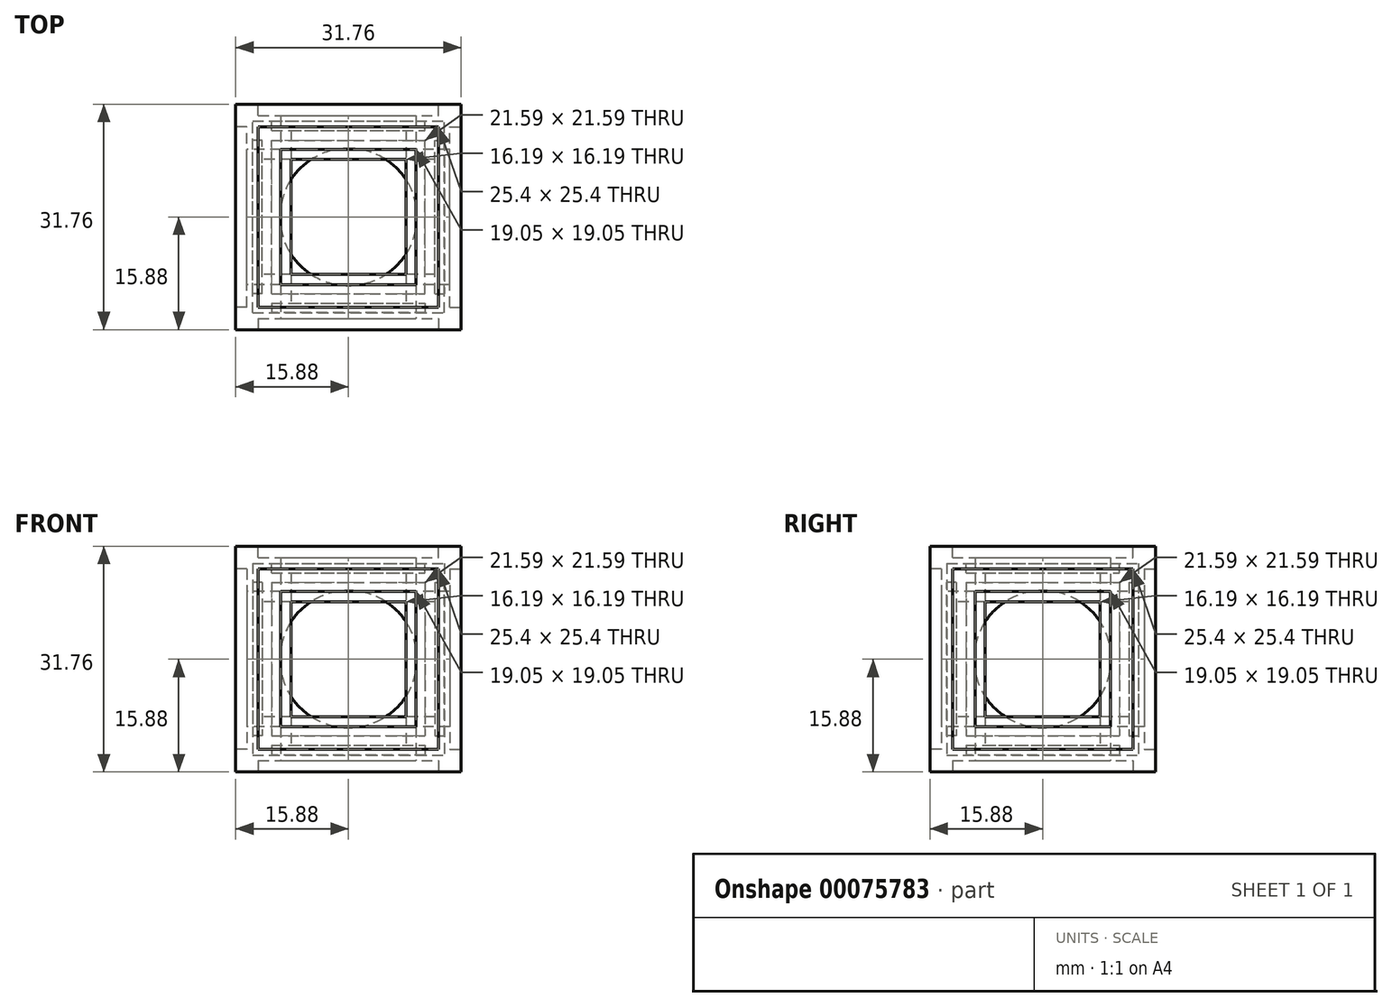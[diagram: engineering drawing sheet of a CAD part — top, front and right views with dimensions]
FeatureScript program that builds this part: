
annotation { "Feature Type Name" : "Feature", "Feature Type Description" : "" }
export const myFeature = defineFeature(function(context is Context, id is Id, definition is map)
    precondition{}
    {
        {
            var Q0;
            Q0=qCreatedBy(makeId("Top.planeOp"),FACE);
            var sketch = newSketch(context, id + "F0", { "sketchPlane" : qUnion([Q0])});
            skLineSegment(sketch, "E0.bottom", {"start": v(0, 0) * mm, "end": v(31.75, 0) * mm});
            skLineSegment(sketch, "E0.top", {"start": v(0, 31.75) * mm, "end": v(31.75, 31.75) * mm});
            skLineSegment(sketch, "E0.left", {"start": v(0, 0) * mm, "end": v(0, 31.75) * mm});
            skLineSegment(sketch, "E0.right", {"start": v(31.75, 0) * mm, "end": v(31.75, 31.75) * mm});
            skSolve(sketch);
        }
        {
            var Q0;
            Q0=makeQuery(id+"F0.imprint","IMPRINT",FACE,{"disambiguationData":[TD([[makeQuery(id+"F0.imprint","IMPRINT",EDGE,{"derivedFrom":sQuery(id+"F0.wireOp",EDGE,"E0.bottom")}),1.0]])]});
            extrude(context, id + "F1", {"entities" : qUnion([Q0]), "depth" : 31.75 * mm});
        }
        {
            var Q0;
            Q0=makeQuery(id+"F1.opExtrude","SWEPT_FACE",FACE,{"disambiguationData":[OSD([sQuery(id+"F0.wireOp",EDGE,"E0.bottom")])]});
            var sketch = newSketch(context, id + "F2", { "sketchPlane" : qUnion([Q0])});
            skLineSegment(sketch, "E1.0", {"start": v(28.57, 28.57) * mm, "end": v(28.57, 3.18) * mm});
            skLineSegment(sketch, "E1.1", {"start": v(3.18, 28.57) * mm, "end": v(28.57, 28.57) * mm});
            skLineSegment(sketch, "E1.2", {"start": v(3.18, 28.57) * mm, "end": v(3.18, 3.18) * mm});
            skLineSegment(sketch, "E1.3", {"start": v(3.18, 3.18) * mm, "end": v(28.57, 3.18) * mm});
            skLineSegment(sketch, "E2.0", {"start": v(25.4, 25.4) * mm, "end": v(25.4, 6.35) * mm});
            skLineSegment(sketch, "E2.1", {"start": v(6.35, 25.4) * mm, "end": v(25.4, 25.4) * mm});
            skLineSegment(sketch, "E2.2", {"start": v(6.35, 25.4) * mm, "end": v(6.35, 6.35) * mm});
            skLineSegment(sketch, "E2.3", {"start": v(6.35, 6.35) * mm, "end": v(25.4, 6.35) * mm});
            skSolve(sketch);
        }
        {
            var Q0;
            Q0=makeQuery(id+"F1.opExtrude","CAP_FACE",FACE,{"disambiguationData":[OSD([sQuery(id+"F0.wireOp",EDGE,"E0.bottom"),sQuery(id+"F0.wireOp",EDGE,"E0.top"),sQuery(id+"F0.wireOp",EDGE,"E0.left"),sQuery(id+"F0.wireOp",EDGE,"E0.right")])],"isStart":false});
            var sketch = newSketch(context, id + "F3", { "sketchPlane" : qUnion([Q0])});
            skLineSegment(sketch, "E3.0", {"start": v(28.58, 3.18) * mm, "end": v(28.57, 28.57) * mm});
            skLineSegment(sketch, "E3.1", {"start": v(3.18, 3.18) * mm, "end": v(28.58, 3.18) * mm});
            skLineSegment(sketch, "E3.2", {"start": v(3.18, 3.18) * mm, "end": v(3.18, 28.57) * mm});
            skLineSegment(sketch, "E3.3", {"start": v(3.18, 28.57) * mm, "end": v(28.57, 28.57) * mm});
            skLineSegment(sketch, "E4.0", {"start": v(6.35, 25.4) * mm, "end": v(25.4, 25.4) * mm});
            skLineSegment(sketch, "E4.1", {"start": v(6.35, 6.35) * mm, "end": v(6.35, 25.4) * mm});
            skLineSegment(sketch, "E4.2", {"start": v(6.35, 6.35) * mm, "end": v(25.4, 6.35) * mm});
            skLineSegment(sketch, "E4.3", {"start": v(25.4, 6.35) * mm, "end": v(25.4, 25.4) * mm});
            skSolve(sketch);
        }
        {
            var Q0;
            Q0=makeQuery(id+"F1.opExtrude","SWEPT_FACE",FACE,{"disambiguationData":[OSD([sQuery(id+"F0.wireOp",EDGE,"E0.right")])]});
            var sketch = newSketch(context, id + "F4", { "sketchPlane" : qUnion([Q0])});
            skLineSegment(sketch, "E5.0", {"start": v(28.57, 28.57) * mm, "end": v(28.57, 3.18) * mm});
            skLineSegment(sketch, "E5.1", {"start": v(3.17, 28.57) * mm, "end": v(28.57, 28.57) * mm});
            skLineSegment(sketch, "E5.2", {"start": v(3.17, 28.57) * mm, "end": v(3.17, 3.18) * mm});
            skLineSegment(sketch, "E5.3", {"start": v(3.17, 3.18) * mm, "end": v(28.57, 3.18) * mm});
            skLineSegment(sketch, "E6.0", {"start": v(25.4, 25.4) * mm, "end": v(25.4, 6.35) * mm});
            skLineSegment(sketch, "E6.1", {"start": v(6.35, 25.4) * mm, "end": v(25.4, 25.4) * mm});
            skLineSegment(sketch, "E6.2", {"start": v(6.35, 25.4) * mm, "end": v(6.35, 6.35) * mm});
            skLineSegment(sketch, "E6.3", {"start": v(6.35, 6.35) * mm, "end": v(25.4, 6.35) * mm});
            skSolve(sketch);
        }
        {
            var Q0;
            Q0=makeQuery(id+"F1.opExtrude","SWEPT_FACE",FACE,{"disambiguationData":[OSD([sQuery(id+"F0.wireOp",EDGE,"E0.top")])]});
            var sketch = newSketch(context, id + "F5", { "sketchPlane" : qUnion([Q0])});
            skLineSegment(sketch, "E7.0", {"start": v(-3.18, 28.57) * mm, "end": v(-3.18, 3.18) * mm});
            skLineSegment(sketch, "E7.1", {"start": v(-3.18, 28.57) * mm, "end": v(-28.57, 28.57) * mm});
            skLineSegment(sketch, "E7.2", {"start": v(-28.57, 28.57) * mm, "end": v(-28.57, 3.18) * mm});
            skLineSegment(sketch, "E7.3", {"start": v(-3.18, 3.18) * mm, "end": v(-28.57, 3.18) * mm});
            skLineSegment(sketch, "E8.0", {"start": v(-6.35, 25.4) * mm, "end": v(-6.35, 6.35) * mm});
            skLineSegment(sketch, "E8.1", {"start": v(-6.35, 25.4) * mm, "end": v(-25.4, 25.4) * mm});
            skLineSegment(sketch, "E8.2", {"start": v(-25.4, 25.4) * mm, "end": v(-25.4, 6.35) * mm});
            skLineSegment(sketch, "E8.3", {"start": v(-6.35, 6.35) * mm, "end": v(-25.4, 6.35) * mm});
            skSolve(sketch);
        }
        {
            var Q0;
            Q0=makeQuery(id+"F1.opExtrude","SWEPT_FACE",FACE,{"disambiguationData":[OSD([sQuery(id+"F0.wireOp",EDGE,"E0.left")])]});
            var sketch = newSketch(context, id + "F6", { "sketchPlane" : qUnion([Q0])});
            skLineSegment(sketch, "E9.0", {"start": v(-3.18, 28.57) * mm, "end": v(-28.57, 28.57) * mm});
            skLineSegment(sketch, "E9.1", {"start": v(-3.18, 28.57) * mm, "end": v(-3.18, 3.18) * mm});
            skLineSegment(sketch, "E9.2", {"start": v(-3.18, 3.18) * mm, "end": v(-28.57, 3.18) * mm});
            skLineSegment(sketch, "E9.3", {"start": v(-28.57, 28.57) * mm, "end": v(-28.57, 3.18) * mm});
            skLineSegment(sketch, "E10.0", {"start": v(-6.35, 25.4) * mm, "end": v(-25.4, 25.4) * mm});
            skLineSegment(sketch, "E10.1", {"start": v(-6.35, 25.4) * mm, "end": v(-6.35, 6.35) * mm});
            skLineSegment(sketch, "E10.2", {"start": v(-6.35, 6.35) * mm, "end": v(-25.4, 6.35) * mm});
            skLineSegment(sketch, "E10.3", {"start": v(-25.4, 25.4) * mm, "end": v(-25.4, 6.35) * mm});
            skSolve(sketch);
        }
        {
            var Q0;
            Q0=makeQuery(id+"F0.imprint","IMPRINT",FACE,{"disambiguationData":[TD([[makeQuery(id+"F0.imprint","IMPRINT",EDGE,{"derivedFrom":sQuery(id+"F0.wireOp",EDGE,"E0.bottom")}),1.0]])]});
            var sketch = newSketch(context, id + "F7", { "sketchPlane" : qUnion([Q0])});
            skLineSegment(sketch, "E11.0", {"start": v(3.18, 3.18) * mm, "end": v(28.58, 3.18) * mm});
            skLineSegment(sketch, "E11.1", {"start": v(3.18, 3.18) * mm, "end": v(3.18, 28.57) * mm});
            skLineSegment(sketch, "E11.2", {"start": v(3.18, 28.57) * mm, "end": v(28.57, 28.57) * mm});
            skLineSegment(sketch, "E11.3", {"start": v(28.58, 3.18) * mm, "end": v(28.57, 28.57) * mm});
            skLineSegment(sketch, "E12.0", {"start": v(6.35, 6.35) * mm, "end": v(25.4, 6.35) * mm});
            skLineSegment(sketch, "E12.1", {"start": v(6.35, 6.35) * mm, "end": v(6.35, 25.4) * mm});
            skLineSegment(sketch, "E12.2", {"start": v(6.35, 25.4) * mm, "end": v(25.4, 25.4) * mm});
            skLineSegment(sketch, "E12.3", {"start": v(25.4, 6.35) * mm, "end": v(25.4, 25.4) * mm});
            skSolve(sketch);
        }
        {
            var Q0;
            Q0=makeQuery(id+"F6.imprint","IMPRINT",FACE,{"disambiguationData":[TD([[makeQuery(id+"F6.imprint","IMPRINT",EDGE,{"derivedFrom":sQuery(id+"F6.wireOp",EDGE,"E10.0")}),1.0]])]});
            extrude(context, id + "F8", {"entities" : qUnion([Q0]), "operationType" : NewBodyOperationType.REMOVE, "endBound" : BoundingType.THROUGH_ALL, "oppositeDirection" : true, "depth" : 25.4 * mm});
        }
        {
            var Q0;
            Q0=makeQuery(id+"F2.imprint","IMPRINT",FACE,{"disambiguationData":[TD([[makeQuery(id+"F2.imprint","IMPRINT",EDGE,{"derivedFrom":sQuery(id+"F2.wireOp",EDGE,"E2.0")}),-1.0]])]});
            extrude(context, id + "F9", {"entities" : qUnion([Q0]), "operationType" : NewBodyOperationType.REMOVE, "endBound" : BoundingType.THROUGH_ALL, "oppositeDirection" : true, "depth" : 25.4 * mm});
        }
        {
            var Q0;
            Q0=makeQuery(id+"F7.imprint","IMPRINT",FACE,{"disambiguationData":[TD([[makeQuery(id+"F7.imprint","IMPRINT",EDGE,{"derivedFrom":sQuery(id+"F7.wireOp",EDGE,"E12.0")}),1.0]])]});
            extrude(context, id + "F10", {"entities" : qUnion([Q0]), "operationType" : NewBodyOperationType.REMOVE, "endBound" : BoundingType.THROUGH_ALL, "depth" : 25.4 * mm});
        }
        {
            var Q0;
            Q0=makeQuery(id+"F2.imprint","IMPRINT",FACE,{"disambiguationData":[TD([[makeQuery(id+"F2.imprint","IMPRINT",EDGE,{"derivedFrom":sQuery(id+"F2.wireOp",EDGE,"E1.0")}),-1.0]])]});
            extrude(context, id + "F11", {"entities" : qUnion([Q0]), "operationType" : NewBodyOperationType.REMOVE, "endBound" : BoundingType.SYMMETRIC, "oppositeDirection" : true, "depth" : 3.17 * mm});
        }
        {
            var Q0;
            Q0=makeQuery(id+"F7.imprint","IMPRINT",FACE,{"disambiguationData":[TD([[makeQuery(id+"F7.imprint","IMPRINT",EDGE,{"derivedFrom":sQuery(id+"F7.wireOp",EDGE,"E11.0")}),1.0]])]});
            extrude(context, id + "F12", {"entities" : qUnion([Q0]), "operationType" : NewBodyOperationType.REMOVE, "endBound" : BoundingType.SYMMETRIC, "depth" : 3.17 * mm});
        }
        {
            var Q0;
            Q0=makeQuery(id+"F3.imprint","IMPRINT",FACE,{"disambiguationData":[TD([[makeQuery(id+"F3.imprint","IMPRINT",EDGE,{"derivedFrom":sQuery(id+"F3.wireOp",EDGE,"E3.0")}),1.0]])]});
            extrude(context, id + "F13", {"entities" : qUnion([Q0]), "operationType" : NewBodyOperationType.REMOVE, "endBound" : BoundingType.SYMMETRIC, "oppositeDirection" : true, "depth" : 3.17 * mm});
        }
        {
            var Q0;
            Q0=makeQuery(id+"F4.imprint","IMPRINT",FACE,{"disambiguationData":[TD([[makeQuery(id+"F4.imprint","IMPRINT",EDGE,{"derivedFrom":sQuery(id+"F4.wireOp",EDGE,"E5.0")}),-1.0]])]});
            extrude(context, id + "F14", {"entities" : qUnion([Q0]), "operationType" : NewBodyOperationType.REMOVE, "endBound" : BoundingType.SYMMETRIC, "oppositeDirection" : true, "depth" : 3.17 * mm});
        }
        {
            var Q0;
            Q0=makeQuery(id+"F5.imprint","IMPRINT",FACE,{"disambiguationData":[TD([[makeQuery(id+"F5.imprint","IMPRINT",EDGE,{"derivedFrom":sQuery(id+"F5.wireOp",EDGE,"E7.0")}),-1.0]])]});
            extrude(context, id + "F15", {"entities" : qUnion([Q0]), "operationType" : NewBodyOperationType.REMOVE, "endBound" : BoundingType.SYMMETRIC, "oppositeDirection" : true, "depth" : 3.17 * mm});
        }
        {
            var Q0;
            Q0=makeQuery(id+"F6.imprint","IMPRINT",FACE,{"disambiguationData":[TD([[makeQuery(id+"F6.imprint","IMPRINT",EDGE,{"derivedFrom":sQuery(id+"F6.wireOp",EDGE,"E9.0")}),1.0]])]});
            extrude(context, id + "F16", {"entities" : qUnion([Q0]), "operationType" : NewBodyOperationType.REMOVE, "endBound" : BoundingType.SYMMETRIC, "oppositeDirection" : true, "depth" : 3.17 * mm});
        }
        {
            var Q0;
            Q0=makeQuery(id+"F1.opExtrude","SWEPT_BODY",BODY,{"disambiguationData":[OSD([sQuery(id+"F0.wireOp",EDGE,"E0.bottom"),sQuery(id+"F0.wireOp",EDGE,"E0.top"),sQuery(id+"F0.wireOp",EDGE,"E0.left"),sQuery(id+"F0.wireOp",EDGE,"E0.right")])]});
            transform(context, id + "F17", {"entities" : qUnion([Q0]), "transformType" : TransformType.TRANSLATION_3D, "dx" : -15.88 * mm, "dy" : -15.88 * mm, "dz" : -15.88 * mm, "makeCopy" : false});
        }
        {
            var Q0;
            Q0=qCreatedBy(makeId("Top.planeOp"),FACE);
            var sketch = newSketch(context, id + "F18", { "sketchPlane" : qUnion([Q0])});
            skArc(sketch, "E13", {"start": v(0, -9.65) * mm, "mid": v(9.65, 0) * mm, "end": v(0, 9.65) * mm});
            skLineSegment(sketch, "E14", {"start": v(0, 9.65) * mm, "end": v(0, -9.65) * mm});
            skSolve(sketch);
        }
        {
            var Q0;
            Q0=makeQuery(id+"F18.imprint","IMPRINT",FACE,{"disambiguationData":[TD([[makeQuery(id+"F18.imprint","IMPRINT",EDGE,{"derivedFrom":sQuery(id+"F18.wireOp",EDGE,"E13")}),1.0]])]});
            var Q1;
            Q1=sQuery(id+"F18.wireOp",EDGE,"E14");
            revolve(context, id + "F19", {"entities" : qUnion([Q0]), "axis" : qUnion([Q1]), "revolveType" : RevolveType.FULL});
        }
        {
            var Q0;
            Q0=makeQuery(id+"F1.opExtrude","SWEPT_BODY",BODY,{"disambiguationData":[OSD([sQuery(id+"F0.wireOp",EDGE,"E0.bottom"),sQuery(id+"F0.wireOp",EDGE,"E0.top"),sQuery(id+"F0.wireOp",EDGE,"E0.left"),sQuery(id+"F0.wireOp",EDGE,"E0.right")])]});
            var Q1;
            Q1=qCreatedBy(makeId("Origin.pointOp"),VERTEX);
            transform(context, id + "F20", {"entities" : qUnion([Q0]), "transformType" : TransformType.SCALE_UNIFORMLY, "scale" : .85, "scalePoint" : qUnion([Q1]), "makeCopy" : true});
        }
    });
